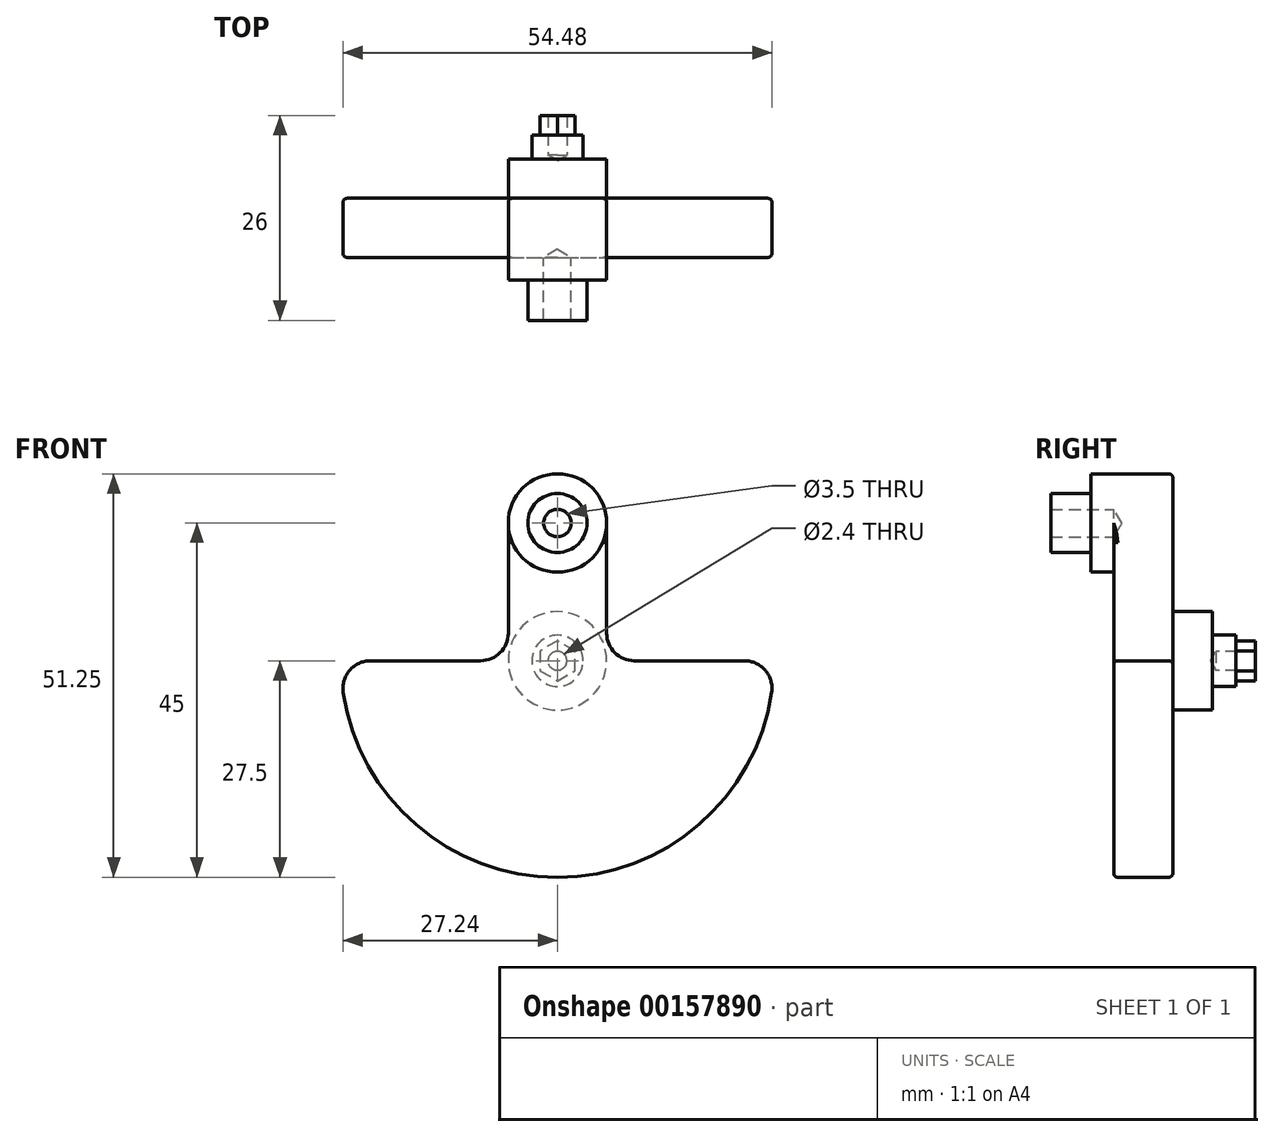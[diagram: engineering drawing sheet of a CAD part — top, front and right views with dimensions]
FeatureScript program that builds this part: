
annotation { "Feature Type Name" : "Feature", "Feature Type Description" : "" }
export const myFeature = defineFeature(function(context is Context, id is Id, definition is map)
    precondition{}
    {
        {
            var Q0;
            Q0=qCreatedBy(makeId("Front.planeOp"),FACE);
            var sketch = newSketch(context, id + "F0", { "sketchPlane" : qUnion([Q0])});
            skLineSegment(sketch, "E0", {"start": v(-6.25, 17.5) * mm, "end": v(-6.25, 3.5) * mm});
            skLineSegment(sketch, "E1", {"start": v(-9.75, 0) * mm, "end": v(-23.74, 0) * mm});
            skLineSegment(sketch, "E2", {"start": v(9.75, 0) * mm, "end": v(23.74, 0) * mm});
            skArc(sketch, "E3", {"start": v(-27.2, -4.01) * mm, "mid": v(0, -27.5) * mm, "end": v(27.2, -4.01) * mm});
            skLineSegment(sketch, "E4", {"start": v(6.25, 3.5) * mm, "end": v(6.25, 17.5) * mm});
            skArc(sketch, "E5", {"start": v(6.25, 17.5) * mm, "mid": v(0, 23.75) * mm, "end": v(-6.25, 17.5) * mm});
            skPoint(sketch, "E6.visualSharp", {"position": v(-6.25, 0) * mm});
            skArc(sketch, "E6.filletArc", {"start": v(-9.75, 0) * mm, "mid": v(-7.28, 1.03) * mm, "end": v(-6.25, 3.5) * mm});
            skPoint(sketch, "E7.visualSharp", {"position": v(6.25, 0) * mm});
            skArc(sketch, "E7.filletArc", {"start": v(6.25, 3.5) * mm, "mid": v(7.28, 1.03) * mm, "end": v(9.75, 0) * mm});
            skPoint(sketch, "E8.visualSharp", {"position": v(-27.5, 0) * mm});
            skArc(sketch, "E8.filletArc", {"start": v(-23.74, 0) * mm, "mid": v(-26.4, -1.21) * mm, "end": v(-27.2, -4.01) * mm});
            skPoint(sketch, "E9.visualSharp", {"position": v(27.5, 0) * mm});
            skArc(sketch, "E9.filletArc", {"start": v(27.2, -4.01) * mm, "mid": v(26.4, -1.21) * mm, "end": v(23.74, 0) * mm});
            skSolve(sketch);
        }
        {
            var Q0;
            Q0 = qSketchRegion(id + "F0", true);
            extrude(context, id + "F1", {"entities" : qUnion([Q0]), "depth" : 7.5 * mm});
        }
        {
            var Q0;
            Q0=makeQuery(id+"F1.opExtrude","CAP_FACE",FACE,{"disambiguationData":[OSD([sQuery(id+"F0.wireOp",EDGE,"E0"),sQuery(id+"F0.wireOp",EDGE,"E1"),sQuery(id+"F0.wireOp",EDGE,"E2"),sQuery(id+"F0.wireOp",EDGE,"E3"),sQuery(id+"F0.wireOp",EDGE,"E4"),sQuery(id+"F0.wireOp",EDGE,"E5"),sQuery(id+"F0.wireOp",EDGE,"E6.filletArc"),sQuery(id+"F0.wireOp",EDGE,"E7.filletArc"),sQuery(id+"F0.wireOp",EDGE,"E8.filletArc"),sQuery(id+"F0.wireOp",EDGE,"E9.filletArc")])],"isStart":false});
            var sketch = newSketch(context, id + "F2", { "sketchPlane" : qUnion([Q0])});
            skCircle(sketch, "E10", {"center": v(0, 17.5) * mm, "radius": 6.25 * mm});
            skCircle(sketch, "E11", {"center": v(0, 17.5) * mm, "radius": 3.75 * mm});
            skSolve(sketch);
        }
        {
            var Q0;
            Q0 = qSketchRegion(id + "F2", true);
            extrude(context, id + "F3", {"entities" : qUnion([Q0]), "operationType" : NewBodyOperationType.ADD, "offsetDistance" : 25 * mm, "depth" : 2.9 * mm});
        }
        {
            var Q0;
            Q0=makeQuery(id+"F3.boolean.opBoolean","SPLIT",FACE,{"disambiguationData":[TD([makeQuery(id+"F3.opExtrude","SWEPT_FACE",FACE,{"disambiguationData":[OSD([sQuery(id+"F2.wireOp",EDGE,"E11")])]})])],"derivedFrom":makeQuery(id+"F1.opExtrude","CAP_FACE",FACE,{"disambiguationData":[OSD([sQuery(id+"F0.wireOp",EDGE,"ThsYxUUj-In8a-KfeX-RcHY-X5HerljZyLpq"),sQuery(id+"F0.wireOp",EDGE,"MEgB8Gsl-571O-v2o0-0gKa-QMTrFAk5mSLA"),sQuery(id+"F0.wireOp",EDGE,"daNeZwNk-dRuE-a8Cp-xYdj-wHWnDJzBArZk.left"),sQuery(id+"F0.wireOp",EDGE,"daNeZwNk-dRuE-a8Cp-xYdj-wHWnDJzBArZk.right"),sQuery(id+"F0.wireOp",EDGE,"YZhJJeg0-epk1-p0Bf-9gle-HjaLlH9S2HiQ"),sQuery(id+"F0.wireOp",EDGE,"a3c9d036-c883-447c-810f-a13d28d4ce0c.trimOffspring"),sQuery(id+"F0.wireOp",EDGE,"456bfbf3-65c0-4bf9-8a6a-70ffcb60a8dd.filletArc"),sQuery(id+"F0.wireOp",EDGE,"e8859686-7351-4259-abec-1b4a687fb985.filletArc"),sQuery(id+"F0.wireOp",EDGE,"a5c384c8-9c9b-4f57-a3a3-591b7f10caef.filletArc"),sQuery(id+"F0.wireOp",EDGE,"6f706540-fc04-4684-bcc6-2744dcb9cc82.filletArc")])],"isStart":false})});
            var Q1;
            Q1=makeQuery(id+"F3.boolean.opBoolean","SPLIT",FACE,{"disambiguationData":[TD([makeQuery(id+"F3.opExtrude","SWEPT_FACE",FACE,{"disambiguationData":[OSD([sQuery(id+"F2.wireOp",EDGE,"E11")])]})])],"derivedFrom":makeQuery(id+"F1.opExtrude","CAP_FACE",FACE,{"disambiguationData":[OSD([sQuery(id+"F0.wireOp",EDGE,"E0"),sQuery(id+"F0.wireOp",EDGE,"E1"),sQuery(id+"F0.wireOp",EDGE,"E2"),sQuery(id+"F0.wireOp",EDGE,"E3"),sQuery(id+"F0.wireOp",EDGE,"E4"),sQuery(id+"F0.wireOp",EDGE,"E5"),sQuery(id+"F0.wireOp",EDGE,"E6.filletArc"),sQuery(id+"F0.wireOp",EDGE,"E7.filletArc"),sQuery(id+"F0.wireOp",EDGE,"E8.filletArc"),sQuery(id+"F0.wireOp",EDGE,"E9.filletArc")])],"isStart":false})});
            extrude(context, id + "F4", {"entities" : qUnion([Q0, Q1]), "operationType" : NewBodyOperationType.ADD, "offsetDistance" : 25 * mm, "depth" : 8 * mm});
        }
        {
            var Q0;
            Q0=makeQuery(id+"F1.opExtrude","CAP_FACE",FACE,{"disambiguationData":[OSD([sQuery(id+"F0.wireOp",EDGE,"E0"),sQuery(id+"F0.wireOp",EDGE,"E1"),sQuery(id+"F0.wireOp",EDGE,"E2"),sQuery(id+"F0.wireOp",EDGE,"E3"),sQuery(id+"F0.wireOp",EDGE,"E4"),sQuery(id+"F0.wireOp",EDGE,"E5"),sQuery(id+"F0.wireOp",EDGE,"E6.filletArc"),sQuery(id+"F0.wireOp",EDGE,"E7.filletArc"),sQuery(id+"F0.wireOp",EDGE,"E8.filletArc"),sQuery(id+"F0.wireOp",EDGE,"E9.filletArc")])],"isStart":true});
            var sketch = newSketch(context, id + "F5", { "sketchPlane" : qUnion([Q0])});
            skCircle(sketch, "E12", {"center": v(0, 0) * mm, "radius": 6.25 * mm});
            skSolve(sketch);
        }
        {
            var Q0;
            Q0 = qSketchRegion(id + "F5", true);
            extrude(context, id + "F6", {"entities" : qUnion([Q0]), "operationType" : NewBodyOperationType.ADD, "offsetDistance" : 25 * mm, "depth" : 5 * mm});
        }
        {
            var Q0;
            Q0=makeQuery(id+"F6.opExtrude","CAP_FACE",FACE,{"disambiguationData":[OSD([sQuery(id+"F5.wireOp",EDGE,"E12")])],"isStart":false});
            var sketch = newSketch(context, id + "F7", { "sketchPlane" : qUnion([Q0])});
            skCircle(sketch, "E13", {"center": v(0, 0) * mm, "radius": 3.25 * mm});
            skSolve(sketch);
        }
        {
            var Q0;
            Q0 = qSketchRegion(id + "F7", true);
            extrude(context, id + "F8", {"entities" : qUnion([Q0]), "operationType" : NewBodyOperationType.ADD, "offsetDistance" : 25 * mm, "depth" : 3 * mm});
        }
        {
            var Q0;
            Q0=makeQuery(id+"F8.opExtrude","CAP_FACE",FACE,{"disambiguationData":[OSD([sQuery(id+"F7.wireOp",EDGE,"E13")])],"isStart":false});
            var sketch = newSketch(context, id + "F9", { "sketchPlane" : qUnion([Q0])});
            skCircle(sketch, "E14.cCircle", {"center": v(0, 0) * mm, "radius": 2.2 * mm, "construction": true});
            skLineSegment(sketch, "E14.0", {"start": v(2.2, 1.27) * mm, "end": v(2.2, -1.27) * mm});
            skLineSegment(sketch, "E14.1", {"start": v(2.2, -1.27) * mm, "end": v(0, -2.54) * mm});
            skLineSegment(sketch, "E14.2", {"start": v(0, -2.54) * mm, "end": v(-2.2, -1.27) * mm});
            skLineSegment(sketch, "E14.3", {"start": v(-2.2, -1.27) * mm, "end": v(-2.2, 1.27) * mm});
            skLineSegment(sketch, "E14.4", {"start": v(-2.2, 1.27) * mm, "end": v(0, 2.54) * mm});
            skLineSegment(sketch, "E14.5", {"start": v(0, 2.54) * mm, "end": v(2.2, 1.27) * mm});
            skPoint(sketch, "E14.0.midPoint", {"position": v(2.2, 0) * mm});
            skSolve(sketch);
        }
        {
            var Q0;
            Q0 = qSketchRegion(id + "F9", true);
            extrude(context, id + "F10", {"entities" : qUnion([Q0]), "operationType" : NewBodyOperationType.ADD, "offsetDistance" : 25 * mm, "depth" : 2.5 * mm});
        }
        {
            var Q0;
            Q0=makeQuery(id+"F1.opExtrude","CAP_EDGE",EDGE,{"disambiguationData":[OSD([sQuery(id+"F0.wireOp",EDGE,"daNeZwNk-dRuE-a8Cp-xYdj-wHWnDJzBArZk.right")])],"isStart":false});
            var Q1;
            Q1=makeQuery(id+"F1.opExtrude","CAP_EDGE",EDGE,{"disambiguationData":[OSD([sQuery(id+"F0.wireOp",EDGE,"ThsYxUUj-In8a-KfeX-RcHY-X5HerljZyLpq")])],"isStart":true});
            var Q2;
            Q2=makeQuery(id+"F1.opExtrude","CAP_EDGE",EDGE,{"disambiguationData":[OSD([sQuery(id+"F0.wireOp",EDGE,"E3")])],"isStart":true});
            var Q3;
            Q3=makeQuery(id+"F1.opExtrude","CAP_EDGE",EDGE,{"disambiguationData":[OSD([sQuery(id+"F0.wireOp",EDGE,"E3")])],"isStart":false});
            fillet(context, id + "F11", {"entities" : qUnion([Q0, Q1, Q2, Q3]), "radius" : 0.5 * mm, "tangentPropagation" : true, "defaultsChanged" : false, "vertexSettings" : [], "allowEdgeOverflow" : false});
        }
        {
            var Q0;
            Q0=makeQuery(id+"F4.opExtrude","CAP_FACE",FACE,{"disambiguationData":[OSD([sQuery(id+"F0.wireOp",EDGE,"E0"),sQuery(id+"F0.wireOp",EDGE,"E1"),sQuery(id+"F0.wireOp",EDGE,"E2"),sQuery(id+"F0.wireOp",EDGE,"E3"),sQuery(id+"F0.wireOp",EDGE,"E4"),sQuery(id+"F0.wireOp",EDGE,"E5"),sQuery(id+"F0.wireOp",EDGE,"E6.filletArc"),sQuery(id+"F0.wireOp",EDGE,"E7.filletArc"),sQuery(id+"F0.wireOp",EDGE,"E8.filletArc"),sQuery(id+"F0.wireOp",EDGE,"E9.filletArc")])],"isStart":false});
            var sketch = newSketch(context, id + "F12", { "sketchPlane" : qUnion([Q0])});
            skCircle(sketch, "E15", {"center": v(0, 17.5) * mm, "radius": 0.8 * mm});
            skSolve(sketch);
        }
        {
            var Q0;
            Q0=sQuery(id+"F12.wireOp",VERTEX,"E15.center");
            var Q1;
            Q1=makeQuery(id+"F1.opExtrude","SWEPT_BODY",BODY,{"disambiguationData":[OSD([sQuery(id+"F0.wireOp",EDGE,"E0"),sQuery(id+"F0.wireOp",EDGE,"E1"),sQuery(id+"F0.wireOp",EDGE,"E2"),sQuery(id+"F0.wireOp",EDGE,"E3"),sQuery(id+"F0.wireOp",EDGE,"E4"),sQuery(id+"F0.wireOp",EDGE,"E5"),sQuery(id+"F0.wireOp",EDGE,"E6.filletArc"),sQuery(id+"F0.wireOp",EDGE,"E7.filletArc"),sQuery(id+"F0.wireOp",EDGE,"E8.filletArc"),sQuery(id+"F0.wireOp",EDGE,"E9.filletArc")])]});
            hole(context, id + "F13", {"style" : HoleStyle.SIMPLE, "endStyle" : HoleEndStyle.BLIND, "holeDiameter" : 3.5 * mm, "majorDiameter" : 5 * mm, "holeDepth" : 8 * mm, "locations" : qUnion([Q0]), "scope" : qUnion([Q1]), "tappedDepth" : 12 * mm, "tapClearance" : 3, "startStyle" : HoleStartStyle.SKETCH});
        }
        {
            var Q0;
            Q0=makeQuery(id+"F10.opExtrude","CAP_FACE",FACE,{"disambiguationData":[OSD([sQuery(id+"F9.wireOp",EDGE,"E14.0"),sQuery(id+"F9.wireOp",EDGE,"E14.1"),sQuery(id+"F9.wireOp",EDGE,"E14.2"),sQuery(id+"F9.wireOp",EDGE,"E14.3"),sQuery(id+"F9.wireOp",EDGE,"E14.4"),sQuery(id+"F9.wireOp",EDGE,"E14.5")])],"isStart":false});
            var sketch = newSketch(context, id + "F14", { "sketchPlane" : qUnion([Q0])});
            skPoint(sketch, "E16", {"position": v(0, 0) * mm});
            skSolve(sketch);
        }
        {
            var Q0;
            Q0=sQuery(id+"F14.wireOp",VERTEX,"E16");
            var Q1;
            Q1=makeQuery(id+"F1.opExtrude","SWEPT_BODY",BODY,{"disambiguationData":[OSD([sQuery(id+"F0.wireOp",EDGE,"E0"),sQuery(id+"F0.wireOp",EDGE,"E1"),sQuery(id+"F0.wireOp",EDGE,"E2"),sQuery(id+"F0.wireOp",EDGE,"E3"),sQuery(id+"F0.wireOp",EDGE,"E4"),sQuery(id+"F0.wireOp",EDGE,"E5"),sQuery(id+"F0.wireOp",EDGE,"E6.filletArc"),sQuery(id+"F0.wireOp",EDGE,"E7.filletArc"),sQuery(id+"F0.wireOp",EDGE,"E8.filletArc"),sQuery(id+"F0.wireOp",EDGE,"E9.filletArc")])]});
            hole(context, id + "F15", {"style" : HoleStyle.SIMPLE, "endStyle" : HoleEndStyle.BLIND, "standardTappedOrClearance" : lookupTablePath({ "standard" : "ISO", "engagement" : "75%", "pitch" : "0.6 mm", "size" : "M3", "type" : "Tapped" }), "standardBlindInLast" : lookupTablePath({ "standard" : "ISO", "engagement" : "75%", "pitch" : "0.6 mm", "size" : "M3", "type" : "Tapped" }), "holeDiameter" : 2.4 * mm, "majorDiameter" : 5 * mm, "holeDepth" : 5 * mm, "locations" : qUnion([Q0]), "scope" : qUnion([Q1]), "tappedDepth" : 12 * mm, "tapClearance" : 3, "startStyle" : HoleStartStyle.SKETCH});
        }
    });
